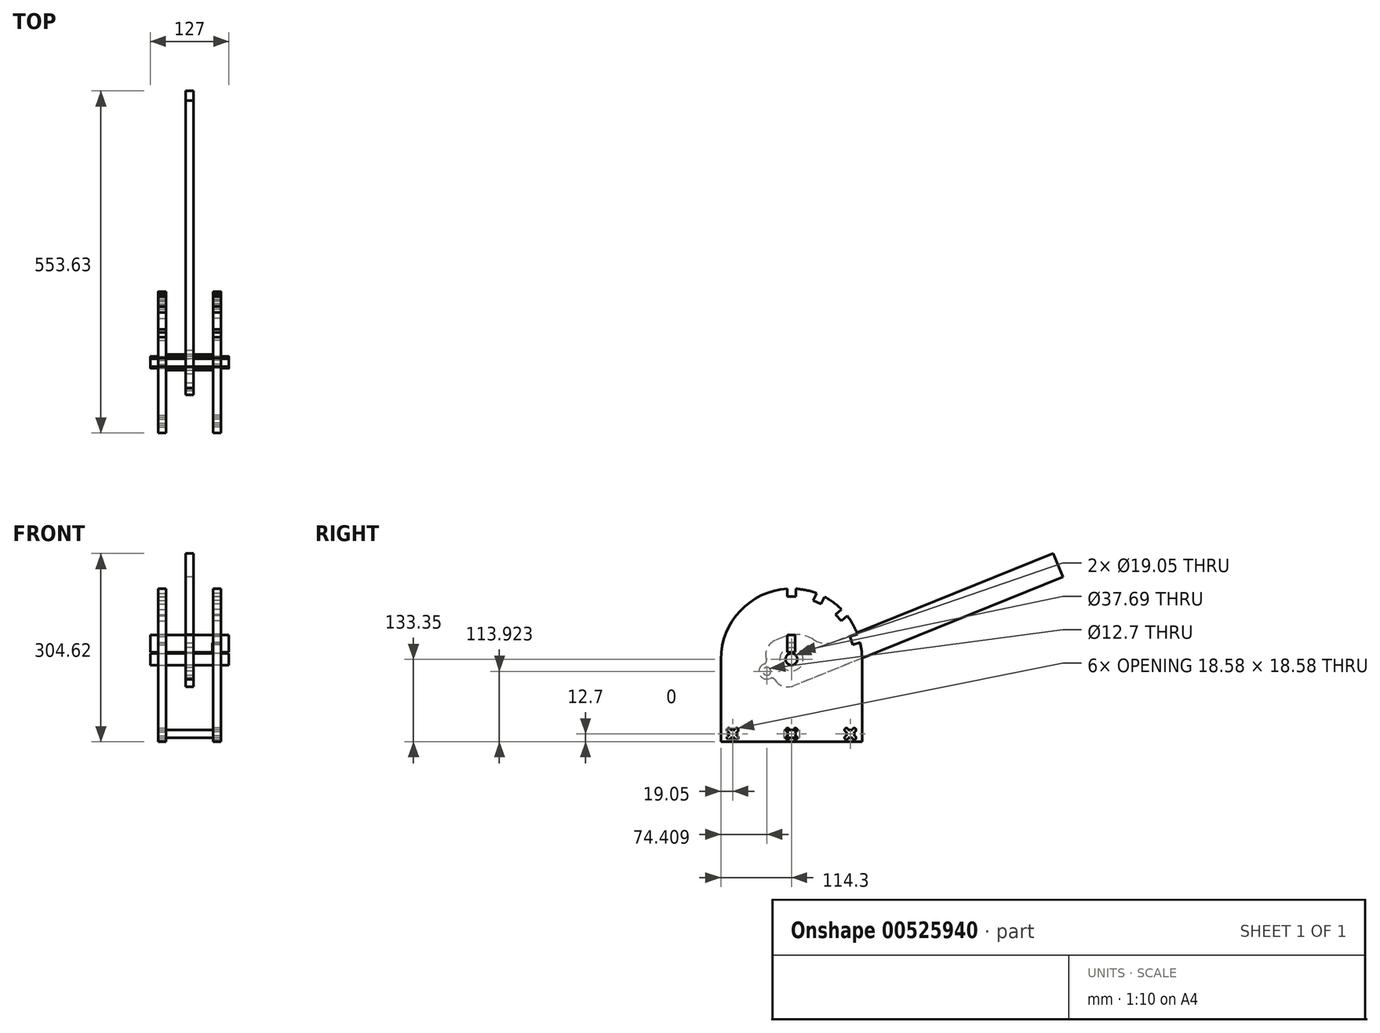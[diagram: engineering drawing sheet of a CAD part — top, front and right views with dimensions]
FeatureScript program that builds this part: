
annotation { "Feature Type Name" : "Feature", "Feature Type Description" : "" }
export const myFeature = defineFeature(function(context is Context, id is Id, definition is map)
    precondition{}
    {
        {
            var Q0;
            Q0=qCreatedBy(makeId("Right.planeOp"),FACE);
            cPlane(context, id + "F0", {"entities" : qUnion([Q0]), "cplaneType" : CPlaneType.OFFSET, "offset" : 38.1 * mm, "width" : 152.4 * mm, "height" : 152.4 * mm});
        }
        {
            var Q0;
            Q0=qCreatedBy(makeId("Right.planeOp"),FACE);
            var sketch = newSketch(context, id + "F1", { "sketchPlane" : qUnion([Q0])});
            skLineSegment(sketch, "E0", {"start": v(0, 127) * mm, "end": v(423.9, 298.27) * mm});
            skLineSegment(sketch, "E1", {"start": v(0, 127) * mm, "end": v(304.8, 127) * mm});
            skLineSegment(sketch, "E2", {"start": v(423.9, 298.27) * mm, "end": v(366.82, 439.57) * mm, "construction": true});
            skLineSegment(sketch, "E3", {"start": v(271.5, 298.27) * mm, "end": v(423.9, 298.27) * mm, "construction": true});
            skLineSegment(sketch, "E4", {"start": v(0, 127) * mm, "end": v(141.28, 561.82) * mm});
            skLineSegment(sketch, "E5", {"start": v(141.28, 561.82) * mm, "end": v(-3.66, 608.92) * mm, "construction": true});
            skLineSegment(sketch, "E6", {"start": v(-11.12, 561.82) * mm, "end": v(141.28, 561.82) * mm, "construction": true});
            skCircle(sketch, "E7", {"center": v(0, 127) * mm, "radius": 12.7 * mm});
            skSolve(sketch);
        }
        {
            var Q0;
            Q0=qCreatedBy(makeId("Right.planeOp"),FACE);
            var sketch = newSketch(context, id + "F2", { "sketchPlane" : qUnion([Q0])});
            skLineSegment(sketch, "E8.bottom", {"start": v(-381, 0) * mm, "end": v(381, 0) * mm});
            skLineSegment(sketch, "E8.top", {"start": v(-381, -25.4) * mm, "end": v(381, -25.4) * mm});
            skLineSegment(sketch, "E8.left", {"start": v(-381, 0) * mm, "end": v(-381, -25.4) * mm});
            skLineSegment(sketch, "E8.right", {"start": v(381, 0) * mm, "end": v(381, -25.4) * mm});
            skLineSegment(sketch, "E9", {"start": v(0, 0) * mm, "end": v(0, -157.3) * mm, "construction": true});
            skSolve(sketch);
        }
        {
            var Q0;
            Q0=qCreatedBy(id+"F0.planeOp",FACE);
            var sketch = newSketch(context, id + "F3", { "sketchPlane" : qUnion([Q0])});
            skLineSegment(sketch, "E10.top", {"start": v(-114.3, 127) * mm, "end": v(114.3, 127) * mm, "construction": true});
            skLineSegment(sketch, "E10.left", {"start": v(-114.3, -6.35) * mm, "end": v(-114.3, 127) * mm});
            skLineSegment(sketch, "E10.right", {"start": v(114.3, -6.35) * mm, "end": v(114.3, 127) * mm});
            skLineSegment(sketch, "E11", {"start": v(0, 127) * mm, "end": v(0, -67.68) * mm, "construction": true});
            skPoint(sketch, "E11.endSnap0", {"position": v(0, 127) * mm});
            skCircle(sketch, "E12", {"center": v(0, 127) * mm, "radius": 9.53 * mm});
            skLineSegment(sketch, "E13", {"start": v(-101.6, 3) * mm, "end": v(-101.6, 9.7) * mm});
            skLineSegment(sketch, "E14", {"start": v(-98.6, 12.7) * mm, "end": v(-91.9, 12.7) * mm});
            skLineSegment(sketch, "E15", {"start": v(-88.9, 9.7) * mm, "end": v(-88.9, 3) * mm});
            skLineSegment(sketch, "E16", {"start": v(101.6, 3) * mm, "end": v(101.6, 9.7) * mm});
            skLineSegment(sketch, "E17", {"start": v(98.6, 12.7) * mm, "end": v(91.9, 12.7) * mm});
            skLineSegment(sketch, "E18", {"start": v(88.9, 9.7) * mm, "end": v(88.9, 3) * mm});
            skLineSegment(sketch, "E19", {"start": v(-6.35, 3) * mm, "end": v(-6.35, 9.7) * mm});
            skLineSegment(sketch, "E20", {"start": v(-3.35, 12.7) * mm, "end": v(3.35, 12.7) * mm});
            skLineSegment(sketch, "E21", {"start": v(6.35, 9.7) * mm, "end": v(6.35, 3) * mm});
            skLineSegment(sketch, "E22", {"start": v(98.6, 0) * mm, "end": v(91.9, 0) * mm});
            skLineSegment(sketch, "E23", {"start": v(3.35, 0) * mm, "end": v(-3.35, 0) * mm});
            skLineSegment(sketch, "E24", {"start": v(-98.6, 0) * mm, "end": v(-91.9, 0) * mm});
            skLineSegment(sketch, "E25", {"start": v(114.3, -6.35) * mm, "end": v(-114.3, -6.35) * mm});
            skPoint(sketch, "E26.orphan", {"position": v(114.3, 0) * mm});
            skPoint(sketch, "E27.orphan", {"position": v(-114.3, 0) * mm});
            skArc(sketch, "E28", {"start": v(-88.9, 9.7) * mm, "mid": v(-86.78, 14.82) * mm, "end": v(-91.9, 12.7) * mm});
            skArc(sketch, "E29", {"start": v(-101.6, 3) * mm, "mid": v(-103.72, -2.12) * mm, "end": v(-98.6, 0) * mm});
            skArc(sketch, "E30", {"start": v(-91.9, 0) * mm, "mid": v(-86.78, -2.12) * mm, "end": v(-88.9, 3) * mm});
            skArc(sketch, "E31", {"start": v(-3.35, 12.7) * mm, "mid": v(-8.47, 14.82) * mm, "end": v(-6.35, 9.7) * mm});
            skArc(sketch, "E32", {"start": v(6.35, 9.7) * mm, "mid": v(8.47, 14.82) * mm, "end": v(3.35, 12.7) * mm});
            skArc(sketch, "E33", {"start": v(-6.35, 3) * mm, "mid": v(-8.47, -2.12) * mm, "end": v(-3.35, 0) * mm});
            skArc(sketch, "E34", {"start": v(3.35, 0) * mm, "mid": v(8.47, -2.12) * mm, "end": v(6.35, 3) * mm});
            skArc(sketch, "E35", {"start": v(91.9, 12.7) * mm, "mid": v(86.78, 14.82) * mm, "end": v(88.9, 9.7) * mm});
            skArc(sketch, "E36", {"start": v(101.6, 9.7) * mm, "mid": v(103.72, 14.82) * mm, "end": v(98.6, 12.7) * mm});
            skArc(sketch, "E37", {"start": v(88.9, 3) * mm, "mid": v(86.78, -2.12) * mm, "end": v(91.9, 0) * mm});
            skArc(sketch, "E38", {"start": v(98.6, 0) * mm, "mid": v(103.72, -2.12) * mm, "end": v(101.6, 3) * mm});
            skArc(sketch, "E39", {"start": v(-98.6, 12.7) * mm, "mid": v(-103.72, 14.82) * mm, "end": v(-101.6, 9.7) * mm});
            skArc(sketch, "E40", {"start": v(114.3, 127) * mm, "mid": v(113.49, 140.6) * mm, "end": v(111.06, 154.01) * mm});
            skLineSegment(sketch, "E41", {"start": v(0, 127) * mm, "end": v(0, 281.9) * mm, "construction": true});
            skLineSegment(sketch, "E42", {"start": v(-6.99, 241.09) * mm, "end": v(-6.99, 228.39) * mm});
            skLineSegment(sketch, "E43", {"start": v(-6.98, 228.39) * mm, "end": v(6.98, 228.39) * mm});
            skLineSegment(sketch, "E44", {"start": v(6.99, 228.39) * mm, "end": v(6.99, 241.09) * mm});
            skLineSegment(sketch, "E45.1.0", {"start": v(48.05, 216.55) * mm, "end": v(53.27, 228.13) * mm});
            skLineSegment(sketch, "E45.1.1", {"start": v(35.31, 222.3) * mm, "end": v(48.05, 216.55) * mm});
            skLineSegment(sketch, "E45.1.2", {"start": v(40.54, 233.87) * mm, "end": v(35.31, 222.3) * mm});
            skLineSegment(sketch, "E45.2.0", {"start": v(80.62, 188.88) * mm, "end": v(90.14, 197.29) * mm});
            skLineSegment(sketch, "E45.2.1", {"start": v(71.37, 199.35) * mm, "end": v(80.62, 188.88) * mm});
            skLineSegment(sketch, "E45.2.2", {"start": v(80.89, 207.76) * mm, "end": v(71.37, 199.35) * mm});
            skLineSegment(sketch, "E45.3.0", {"start": v(98.93, 150.26) * mm, "end": v(111.06, 154.01) * mm});
            skLineSegment(sketch, "E45.3.1", {"start": v(94.8, 163.61) * mm, "end": v(98.93, 150.26) * mm});
            skLineSegment(sketch, "E45.3.2", {"start": v(106.94, 167.36) * mm, "end": v(94.8, 163.61) * mm});
            skLineSegment(sketch, "E45.anchor1", {"start": v(0, 127) * mm, "end": v(-6.98, 228.39) * mm, "construction": true});
            skLineSegment(sketch, "E45.anchor2", {"start": v(0, 127) * mm, "end": v(94.8, 163.61) * mm, "construction": true});
            skArc(sketch, "E46.trimOffspring", {"start": v(-6.99, 241.09) * mm, "mid": v(-83.26, 205.31) * mm, "end": v(-114.3, 127) * mm});
            skArc(sketch, "E47.trimOffspring", {"start": v(40.54, 233.87) * mm, "mid": v(24.03, 238.74) * mm, "end": v(6.99, 241.09) * mm});
            skArc(sketch, "E48.trimOffspring", {"start": v(80.89, 207.76) * mm, "mid": v(67.85, 218.98) * mm, "end": v(53.27, 228.13) * mm});
            skArc(sketch, "E49.trimOffspring", {"start": v(106.94, 167.36) * mm, "mid": v(99.67, 182.96) * mm, "end": v(90.14, 197.29) * mm});
            skSolve(sketch);
        }
        {
            var Q0;
            Q0=makeQuery(id+"F3.imprint","IMPRINT",FACE,{"disambiguationData":[TD([[makeQuery(id+"F3.imprint","IMPRINT",EDGE,{"derivedFrom":sQuery(id+"F3.wireOp",EDGE,"E10.left")}),-1.0]])]});
            extrude(context, id + "F4", {"entities" : qUnion([Q0]), "depth" : 12.7 * mm, "offsetDistance" : 25.4 * mm});
        }
        {
            var Q0;
            Q0=makeQuery(id+"F4.opExtrude","SWEPT_BODY",BODY,{"disambiguationData":[OSD([sQuery(id+"F3.wireOp",EDGE,"E10.bottom"),sQuery(id+"F3.wireOp",EDGE,"E10.left"),sQuery(id+"F3.wireOp",EDGE,"E10.right"),sQuery(id+"F3.wireOp",EDGE,"eni3YDas-Z2jY-kUTw-0sSa-zKqCjRRRc3TL"),sQuery(id+"F3.wireOp",EDGE,"E12"),sQuery(id+"F3.wireOp",EDGE,"DoDtIKa2-UhQa-ew8c-BZRx-imkwlSQ4y86Z"),sQuery(id+"F3.wireOp",EDGE,"kxvzkePM-JObx-Uu0i-tyUj-t9ebLupwRFWd"),sQuery(id+"F3.wireOp",EDGE,"vxHlAIAC-rk9y-JXcx-1u3x-U7ptDzpiz7Ww"),sQuery(id+"F3.wireOp",EDGE,"a27e66f8-ee90-4248-8e61-52cf080fd80a.1.0"),sQuery(id+"F3.wireOp",EDGE,"a27e66f8-ee90-4248-8e61-52cf080fd80a.1.2"),sQuery(id+"F3.wireOp",EDGE,"a27e66f8-ee90-4248-8e61-52cf080fd80a.1.4"),sQuery(id+"F3.wireOp",EDGE,"a27e66f8-ee90-4248-8e61-52cf080fd80a.2.0"),sQuery(id+"F3.wireOp",EDGE,"a27e66f8-ee90-4248-8e61-52cf080fd80a.2.2"),sQuery(id+"F3.wireOp",EDGE,"a27e66f8-ee90-4248-8e61-52cf080fd80a.2.4"),sQuery(id+"F3.wireOp",EDGE,"a27e66f8-ee90-4248-8e61-52cf080fd80a.3.0"),sQuery(id+"F3.wireOp",EDGE,"a27e66f8-ee90-4248-8e61-52cf080fd80a.3.2"),sQuery(id+"F3.wireOp",EDGE,"a27e66f8-ee90-4248-8e61-52cf080fd80a.3.4"),sQuery(id+"F3.wireOp",EDGE,"a27e66f8-ee90-4248-8e61-52cf080fd80a.4.0"),sQuery(id+"F3.wireOp",EDGE,"a27e66f8-ee90-4248-8e61-52cf080fd80a.4.2"),sQuery(id+"F3.wireOp",EDGE,"a27e66f8-ee90-4248-8e61-52cf080fd80a.4.4"),sQuery(id+"F3.wireOp",EDGE,"a27e66f8-ee90-4248-8e61-52cf080fd80a.5.0"),sQuery(id+"F3.wireOp",EDGE,"a27e66f8-ee90-4248-8e61-52cf080fd80a.5.2"),sQuery(id+"F3.wireOp",EDGE,"a27e66f8-ee90-4248-8e61-52cf080fd80a.5.4"),sQuery(id+"F3.wireOp",EDGE,"a27e66f8-ee90-4248-8e61-52cf080fd80a.6.0"),sQuery(id+"F3.wireOp",EDGE,"a27e66f8-ee90-4248-8e61-52cf080fd80a.6.2"),sQuery(id+"F3.wireOp",EDGE,"a27e66f8-ee90-4248-8e61-52cf080fd80a.6.4"),sQuery(id+"F3.wireOp",EDGE,"a27e66f8-ee90-4248-8e61-52cf080fd80a.7.0"),sQuery(id+"F3.wireOp",EDGE,"a27e66f8-ee90-4248-8e61-52cf080fd80a.7.2"),sQuery(id+"F3.wireOp",EDGE,"a27e66f8-ee90-4248-8e61-52cf080fd80a.7.4"),sQuery(id+"F3.wireOp",EDGE,"a27e66f8-ee90-4248-8e61-52cf080fd80a.8.0"),sQuery(id+"F3.wireOp",EDGE,"a27e66f8-ee90-4248-8e61-52cf080fd80a.8.2"),sQuery(id+"F3.wireOp",EDGE,"a27e66f8-ee90-4248-8e61-52cf080fd80a.8.4"),sQuery(id+"F3.wireOp",EDGE,"a27e66f8-ee90-4248-8e61-52cf080fd80a.9.0"),sQuery(id+"F3.wireOp",EDGE,"a27e66f8-ee90-4248-8e61-52cf080fd80a.9.2"),sQuery(id+"F3.wireOp",EDGE,"a27e66f8-ee90-4248-8e61-52cf080fd80a.9.4"),sQuery(id+"F3.wireOp",EDGE,"8e12a071-d5c6-4a52-bf98-7ce987de2b66.trimOffspring"),sQuery(id+"F3.wireOp",EDGE,"2a0c056e-81ea-4f47-a407-1e20577b0329.trimOffspring"),sQuery(id+"F3.wireOp",EDGE,"9d9dd8ad-a1c3-4744-96de-6e434ef9403d.trimOffspring"),sQuery(id+"F3.wireOp",EDGE,"15600256-a26a-4c16-a253-10ecf8d6f36c.trimOffspring"),sQuery(id+"F3.wireOp",EDGE,"00cff1ab-6678-41c1-9c6b-146366ff7047.trimOffspring"),sQuery(id+"F3.wireOp",EDGE,"56b7ce25-eca8-485c-bfb7-0a9fbca996c9.trimOffspring"),sQuery(id+"F3.wireOp",EDGE,"48b037e2-d6de-4f9a-a15f-27cedd50a077.trimOffspring"),sQuery(id+"F3.wireOp",EDGE,"6380022b-cd75-4d3e-b4a3-29a499a61952.trimOffspring"),sQuery(id+"F3.wireOp",EDGE,"b3e6f2c8-4f6d-48e1-a389-8ae73636b909.trimOffspring"),sQuery(id+"F3.wireOp",EDGE,"84f845ca-c682-4064-afb9-24734b0a5d23.trimOffspring"),sQuery(id+"F3.wireOp",EDGE,"E13"),sQuery(id+"F3.wireOp",EDGE,"E14"),sQuery(id+"F3.wireOp",EDGE,"E15"),sQuery(id+"F3.wireOp",EDGE,"11bb4bb9-3500-4a41-acba-9d245b9ff765.trimOffspring"),sQuery(id+"F3.wireOp",EDGE,"E16"),sQuery(id+"F3.wireOp",EDGE,"E17"),sQuery(id+"F3.wireOp",EDGE,"E18"),sQuery(id+"F3.wireOp",EDGE,"b59c6307-d873-4a57-acc7-1e0ce9fe817d.trimOffspring"),sQuery(id+"F3.wireOp",EDGE,"E19"),sQuery(id+"F3.wireOp",EDGE,"E20"),sQuery(id+"F3.wireOp",EDGE,"E21"),sQuery(id+"F3.wireOp",EDGE,"e3ca75d7-debf-4bac-a9ba-76531b282dc1.trimOffspring")])]});
            var Q1;
            Q1=qCreatedBy(makeId("Right.planeOp"),FACE);
            mirror(context, id + "F5", {"entities" : qUnion([Q0]), "mirrorPlane" : qUnion([Q1])});
        }
        {
            var Q0;
            Q0=qCreatedBy(makeId("Right.planeOp"),FACE);
            var sketch = newSketch(context, id + "F6", { "sketchPlane" : qUnion([Q0])});
            skCircle(sketch, "E50", {"center": v(0, 127) * mm, "radius": 9.53 * mm});
            skSolve(sketch);
        }
        {
            var Q0;
            Q0 = qSketchRegion(id + "F6", true);
            extrude(context, id + "F7", {"entities" : qUnion([Q0]), "depth" : 63.5 * mm, "offsetDistance" : 25.4 * mm, "hasSecondDirection" : true, "secondDirectionOppositeDirection" : true, "secondDirectionDepth" : 63.5 * mm});
        }
        {
            var Q0;
            Q0=qCreatedBy(makeId("Top.planeOp"),FACE);
            var sketch = newSketch(context, id + "F8", { "sketchPlane" : qUnion([Q0])});
            skLineSegment(sketch, "E51", {"start": v(-38.1, -12.7) * mm, "end": v(38.1, -12.7) * mm});
            skLineSegment(sketch, "E52", {"start": v(-38.1, -12.7) * mm, "end": v(-38.1, -6.35) * mm});
            skLineSegment(sketch, "E53", {"start": v(38.1, -12.7) * mm, "end": v(38.1, -6.35) * mm});
            skLineSegment(sketch, "E54", {"start": v(38.1, -6.35) * mm, "end": v(50.8, -6.35) * mm});
            skLineSegment(sketch, "E55", {"start": v(50.8, -6.35) * mm, "end": v(50.8, 6.35) * mm});
            skLineSegment(sketch, "E56", {"start": v(50.8, 6.35) * mm, "end": v(38.1, 6.35) * mm});
            skLineSegment(sketch, "E57", {"start": v(38.1, 6.35) * mm, "end": v(38.1, 12.7) * mm});
            skLineSegment(sketch, "E58", {"start": v(-38.1, -6.35) * mm, "end": v(-50.8, -6.35) * mm});
            skLineSegment(sketch, "E59", {"start": v(-50.8, -6.35) * mm, "end": v(-50.8, 6.35) * mm});
            skLineSegment(sketch, "E60", {"start": v(-50.8, 6.35) * mm, "end": v(-38.1, 6.35) * mm});
            skLineSegment(sketch, "E61", {"start": v(-38.1, 6.35) * mm, "end": v(-38.1, 12.7) * mm});
            skLineSegment(sketch, "E62", {"start": v(38.1, 12.7) * mm, "end": v(-38.1, 12.7) * mm});
            skSolve(sketch);
        }
        {
            var Q0;
            Q0 = qSketchRegion(id + "F8", true);
            extrude(context, id + "F9", {"entities" : qUnion([Q0]), "depth" : 12.7 * mm, "offsetDistance" : 25.4 * mm});
        }
        {
            var Q0;
            Q0=makeQuery(id+"F4.opExtrude","SWEPT_FACE",FACE,{"disambiguationData":[OSD([sQuery(id+"F3.wireOp",EDGE,"E42")])]});
            var sketch = newSketch(context, id + "F10", { "sketchPlane" : qUnion([Q0])});
            skLineSegment(sketch, "E63", {"start": v(38.1, 153.93) * mm, "end": v(38.1, 138.23) * mm});
            skLineSegment(sketch, "E64", {"start": v(38.1, 138.23) * mm, "end": v(-36.83, 138.23) * mm});
            skLineSegment(sketch, "E65", {"start": v(-36.83, 138.23) * mm, "end": v(-36.83, 153.93) * mm});
            skLineSegment(sketch, "E66", {"start": v(-36.83, 153.93) * mm, "end": v(-50.8, 153.93) * mm});
            skLineSegment(sketch, "E67", {"start": v(-50.8, 153.93) * mm, "end": v(-50.8, 138.23) * mm});
            skLineSegment(sketch, "E68", {"start": v(-50.8, 138.23) * mm, "end": v(-63.5, 138.23) * mm});
            skLineSegment(sketch, "E69", {"start": v(-63.5, 138.23) * mm, "end": v(-63.5, 166.63) * mm});
            skLineSegment(sketch, "E70", {"start": v(-63.5, 166.63) * mm, "end": v(63.5, 166.63) * mm});
            skLineSegment(sketch, "E71", {"start": v(63.5, 166.63) * mm, "end": v(63.5, 138.23) * mm});
            skLineSegment(sketch, "E72", {"start": v(63.5, 138.23) * mm, "end": v(50.8, 138.23) * mm});
            skLineSegment(sketch, "E73", {"start": v(50.8, 138.23) * mm, "end": v(50.8, 153.93) * mm});
            skLineSegment(sketch, "E74", {"start": v(50.8, 153.93) * mm, "end": v(38.1, 153.93) * mm});
            skSolve(sketch);
        }
        {
            var Q0;
            Q0=makeQuery(id+"F10.imprint","IMPRINT",FACE,{"disambiguationData":[TD([[makeQuery(id+"F10.imprint","IMPRINT",EDGE,{"derivedFrom":sQuery(id+"F10.wireOp",EDGE,"E63")}),-1.0]])]});
            var Q1;
            {var subQ0=sQuery(id+"F10.wireOp",EDGE,"E71");Q1=makeQuery(id+"F10.imprint","IMPRINT",FACE,{"disambiguationData":[TD([[makeQuery(id+"F10.imprint","IMPRINT",EDGE,{"derivedFrom":subQ0}),-1.0]])]});}
            var Q2;
            Q2=makeQuery(id+"F10.imprint","IMPRINT",FACE,{"disambiguationData":[TD([[makeQuery(id+"F10.imprint","IMPRINT",EDGE,{"derivedFrom":sQuery(id+"F10.wireOp",EDGE,"E74")}),-1.0]])]});
            var Q3;
            {var subQ1=sQuery(id+"F3.wireOp",EDGE,"vxHlAIAC-rk9y-JXcx-1u3x-U7ptDzpiz7Ww");var subQ2=makeQuery(id+"F4.opExtrude","CAP_EDGE",EDGE,{"disambiguationData":[OSD([subQ1])],"isStart":true});Q3=makeQuery(id+"F10.imprint","IMPRINT",FACE,{"disambiguationData":[TD([[makeQuery(id+"F10.imprint","IMPRINT",EDGE,{"derivedFrom":subQ2}),-1.0]])]});}
            extrude(context, id + "F11", {"entities" : qUnion([Q0, Q1, Q2, Q3]), "depth" : 12.7 * mm, "offsetDistance" : 25.4 * mm});
        }
        {
            var Q0;
            Q0=qCreatedBy(makeId("Right.planeOp"),FACE);
            var sketch = newSketch(context, id + "F12", { "sketchPlane" : qUnion([Q0])});
            skCircle(sketch, "E75", {"center": v(0, 127) * mm, "radius": 18.85 * mm});
            skLineSegment(sketch, "E76", {"start": v(423.9, 298.27) * mm, "end": v(439.33, 260.1) * mm});
            skLineSegment(sketch, "E77", {"start": v(-11.26, 163.54) * mm, "end": v(-26.05, 157.57) * mm});
            skLineSegment(sketch, "E78", {"start": v(439.33, 260.1) * mm, "end": v(3.82, 84.14) * mm});
            skPoint(sketch, "E79.visualSharp", {"position": v(-49.6, 148.05) * mm});
            skArc(sketch, "E79.filletArc", {"start": v(-26.05, 157.57) * mm, "mid": v(-39.57, 144.7) * mm, "end": v(-40.66, 126.08) * mm});
            skPoint(sketch, "E80.visualSharp", {"position": v(-19.73, 74.63) * mm});
            skArc(sketch, "E80.filletArc", {"start": v(-27.33, 94.38) * mm, "mid": v(-13.63, 83.56) * mm, "end": v(3.82, 84.14) * mm});
            skLineSegment(sketch, "E81", {"start": v(423.9, 298.27) * mm, "end": v(70.65, 155.55) * mm});
            skLineSegment(sketch, "E82", {"start": v(21.05, 176.6) * mm, "end": v(21.05, 176.6) * mm});
            skPoint(sketch, "E83.orphan", {"position": v(409.64, 333.6) * mm});
            skPoint(sketch, "E84.visualSharp", {"position": v(35.33, 141.27) * mm});
            skArc(sketch, "E84.filletArc", {"start": v(35.54, 158.97) * mm, "mid": v(52.68, 152.95) * mm, "end": v(70.65, 155.55) * mm});
            skPoint(sketch, "E85.visualSharp", {"position": v(21.05, 176.6) * mm});
            skArc(sketch, "E85.filletArc", {"start": v(35.54, 158.97) * mm, "mid": v(12.7, 167) * mm, "end": v(-11.26, 163.54) * mm});
            skLineSegment(sketch, "E86", {"start": v(-43.58, 119.78) * mm, "end": v(-44.65, 119.35) * mm});
            skLineSegment(sketch, "E87", {"start": v(-51.67, 102.82) * mm, "end": v(-51.67, 102.82) * mm});
            skLineSegment(sketch, "E88", {"start": v(-35.13, 95.8) * mm, "end": v(-33.56, 96.43) * mm});
            skPoint(sketch, "E89.visualSharp", {"position": v(-38.76, 121.73) * mm});
            skArc(sketch, "E89.filletArc", {"start": v(-43.58, 119.78) * mm, "mid": v(-40.88, 122.35) * mm, "end": v(-40.66, 126.08) * mm});
            skPoint(sketch, "E90.visualSharp", {"position": v(-29.25, 98.18) * mm});
            skArc(sketch, "E90.filletArc", {"start": v(-27.33, 94.38) * mm, "mid": v(-30.07, 96.55) * mm, "end": v(-33.56, 96.43) * mm});
            skPoint(sketch, "E91.visualSharp", {"position": v(-46.9, 91.04) * mm});
            skArc(sketch, "E91.filletArc", {"start": v(-51.67, 102.82) * mm, "mid": v(-44.85, 95.88) * mm, "end": v(-35.13, 95.8) * mm});
            skPoint(sketch, "E92.visualSharp", {"position": v(-56.42, 114.6) * mm});
            skArc(sketch, "E92.filletArc", {"start": v(-44.65, 119.35) * mm, "mid": v(-51.58, 112.54) * mm, "end": v(-51.67, 102.82) * mm});
            skLineSegment(sketch, "E93", {"start": v(-51.67, 102.82) * mm, "end": v(-27.08, 112.75) * mm, "construction": true});
            skCircle(sketch, "E94", {"center": v(-39.9, 107.57) * mm, "radius": 6.35 * mm});
            skSolve(sketch);
        }
        {
            var Q0;
            Q0=makeQuery(id+"F12.imprint","IMPRINT",FACE,{"disambiguationData":[TD([[makeQuery(id+"F12.imprint","IMPRINT",EDGE,{"derivedFrom":sQuery(id+"F12.wireOp",EDGE,"E75")}),-1.0]])]});
            extrude(context, id + "F13", {"entities" : qUnion([Q0]), "depth" : 6.35 * mm, "offsetDistance" : 25.4 * mm, "hasSecondDirection" : true, "secondDirectionOppositeDirection" : true, "secondDirectionDepth" : 6.35 * mm});
        }
    });
